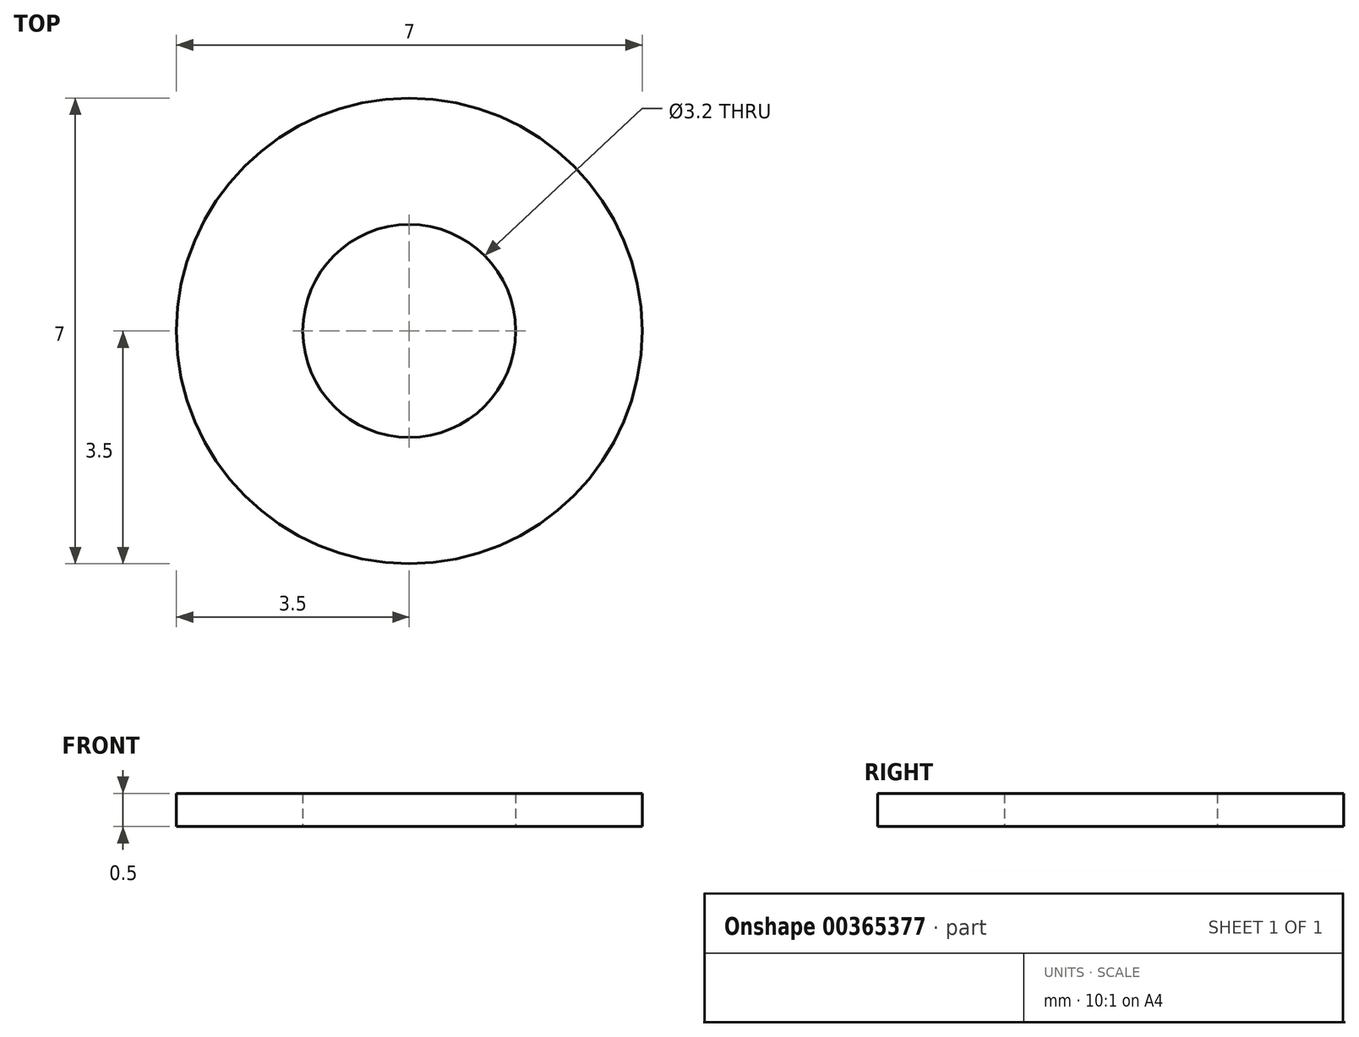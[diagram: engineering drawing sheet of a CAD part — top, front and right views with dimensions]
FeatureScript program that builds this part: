
annotation { "Feature Type Name" : "Feature", "Feature Type Description" : "" }
export const myFeature = defineFeature(function(context is Context, id is Id, definition is map)
    precondition{}
    {
        {
            var Q0;
            Q0=qCreatedBy(makeId("Top.planeOp"),FACE);
            var sketch = newSketch(context, id + "F0", { "sketchPlane" : qUnion([Q0])});
            skCircle(sketch, "E0", {"center": v(0, 0) * mm, "radius": 1.6 * mm});
            skCircle(sketch, "E1", {"center": v(0, 0) * mm, "radius": 3.5 * mm});
            skSolve(sketch);
        }
        {
            var Q0;
            Q0=qSketchRegion(id+"F0",true);
            extrude(context, id + "F1", {"entities" : qUnion([Q0]), "depth" : .5 * mm});
        }
    });
